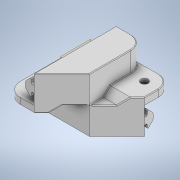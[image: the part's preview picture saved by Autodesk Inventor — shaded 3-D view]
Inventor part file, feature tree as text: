
AUTODESK INVENTOR PART (.ipt)
format: ipt  version: 2020 (Build 240168000, 168)  size: 279,552 bytes
history: native  units: in
note: dims shown in document units (in); Inventor stores cm internally (conversion verified against a paired STEP export)
features: sketch x7, other x3, plane x1
ambient origin geometry x8: Origin, YZ Plane, XZ Plane, XY Plane, X Axis, Y Axis, Z Axis, Center Point
bodies: Solid1 (feature_tree)
feature tree (11):
  other  "90DegJoiner.ipt"
  other  "Solid1::90DegJoiner.ipt"
  other  "TaggingFeature1"
  sketch  "Sketch1"  dims[d0=0.3937in]
  sketch  "Sketch2"
  sketch  "Sketch3"
  sketch  "Sketch4"
  sketch  "Sketch5"
  sketch  "Sketch7"
  sketch  "Sketch8"
  plane  "Work Plane1"
